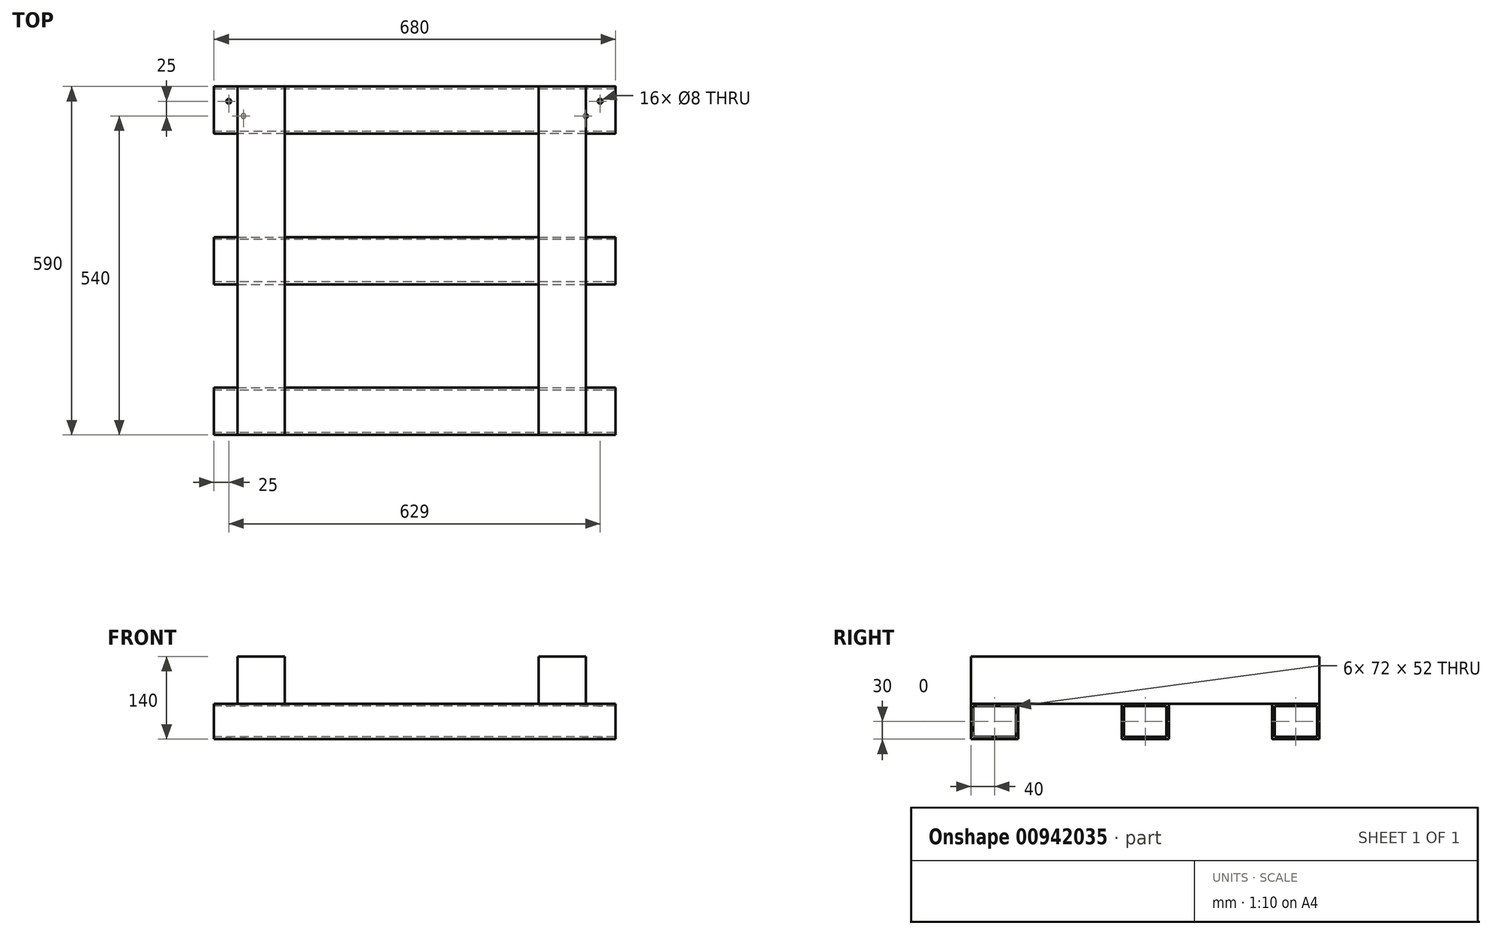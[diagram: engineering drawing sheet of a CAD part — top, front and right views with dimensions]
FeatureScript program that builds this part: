
annotation { "Feature Type Name" : "Feature", "Feature Type Description" : "" }
export const myFeature = defineFeature(function(context is Context, id is Id, definition is map)
    precondition{}
    {
        {
            var Q0;
            Q0=qCreatedBy(makeId("Right.planeOp"),FACE);
            var sketch = newSketch(context, id + "F0", { "sketchPlane" : qUnion([Q0])});
            skLineSegment(sketch, "E0.bottom", {"start": v(40, 30) * mm, "end": v(-40, 30) * mm});
            skLineSegment(sketch, "E0.top", {"start": v(40, -30) * mm, "end": v(-40, -30) * mm});
            skLineSegment(sketch, "E0.left", {"start": v(40, 30) * mm, "end": v(40, -30) * mm});
            skLineSegment(sketch, "E0.right", {"start": v(-40, 30) * mm, "end": v(-40, -30) * mm});
            skPoint(sketch, "E0.middle", {"position": v(0, 0) * mm});
            skSolve(sketch);
        }
        {
            var Q0;
            Q0=qCreatedBy(makeId("Right.planeOp"),FACE);
            var sketch = newSketch(context, id + "F1", { "sketchPlane" : qUnion([Q0])});
            skLineSegment(sketch, "E1.bottom", {"start": v(36, 26) * mm, "end": v(-36, 26) * mm});
            skLineSegment(sketch, "E1.top", {"start": v(36, -26) * mm, "end": v(-36, -26) * mm});
            skLineSegment(sketch, "E1.left", {"start": v(36, 26) * mm, "end": v(36, -26) * mm});
            skLineSegment(sketch, "E1.right", {"start": v(-36, 26) * mm, "end": v(-36, -26) * mm});
            skPoint(sketch, "E1.middle", {"position": v(0, 0) * mm});
            skSolve(sketch);
        }
        {
            var Q0;
            Q0 = qSketchRegion(id + "F0", true);
            extrude(context, id + "F2", {"entities" : qUnion([Q0]), "depth" : 680 * mm, "offsetDistance" : 25.4 * mm});
        }
        {
            var Q0;
            Q0 = qSketchRegion(id + "F1", true);
            extrude(context, id + "F3", {"entities" : qUnion([Q0]), "operationType" : NewBodyOperationType.REMOVE, "endBound" : BoundingType.THROUGH_ALL, "depth" : 600 * mm, "offsetDistance" : 25.4 * mm});
        }
        {
            var Q0;
            Q0=makeQuery(id+"F2.opExtrude","SWEPT_FACE",FACE,{"disambiguationData":[OSD([sQuery(id+"F0.wireOp",EDGE,"E0.right")])]});
            var Q1;
            Q1=makeQuery(id+"F2.opExtrude","SWEPT_FACE",FACE,{"disambiguationData":[OSD([sQuery(id+"F0.wireOp",EDGE,"E0.bottom")])]});
            var Q2;
            Q2=makeQuery(id+"F2.opExtrude","SWEPT_EDGE",EDGE,{"disambiguationData":[OSD([sQuery(id+"F0.wireOp",EDGE,"E0.bottom"),sQuery(id+"F0.wireOp",EDGE,"E0.right")])]});
            var Q3;
            Q3=makeQuery(id+"F2.opExtrude","SWEPT_EDGE",EDGE,{"disambiguationData":[OSD([sQuery(id+"F0.wireOp",EDGE,"E0.bottom"),sQuery(id+"F0.wireOp",EDGE,"E0.left")])]});
            var Q4;
            Q4=makeQuery(id+"F2.opExtrude","SWEPT_EDGE",EDGE,{"disambiguationData":[OSD([sQuery(id+"F0.wireOp",EDGE,"E0.top"),sQuery(id+"F0.wireOp",EDGE,"E0.right")])]});
            var Q5;
            Q5=makeQuery(id+"F2.opExtrude","SWEPT_EDGE",EDGE,{"disambiguationData":[OSD([sQuery(id+"F0.wireOp",EDGE,"E0.top"),sQuery(id+"F0.wireOp",EDGE,"E0.left")])]});
            fillet(context, id + "F4", {"entities" : qUnion([Q0, Q1, Q2, Q3, Q4, Q5]), "radius" : 1 * mm, "tangentPropagation" : true, "allowEdgeOverflow" : false});
        }
        {
            var Q0;
            Q0=makeQuery(id+"F2.opExtrude","SWEPT_FACE",FACE,{"disambiguationData":[OSD([sQuery(id+"F0.wireOp",EDGE,"E0.bottom")])]});
            var sketch = newSketch(context, id + "F5", { "sketchPlane" : qUnion([Q0])});
            skCircle(sketch, "E2", {"center": v(25, 15) * mm, "radius": 4 * mm});
            skCircle(sketch, "E3", {"center": v(50, -10) * mm, "radius": 4 * mm});
            skCircle(sketch, "E4", {"center": v(654, 15) * mm, "radius": 4 * mm});
            skCircle(sketch, "E5", {"center": v(629, -10) * mm, "radius": 4 * mm});
            skSolve(sketch);
        }
        {
            var Q0;
            Q0 = qSketchRegion(id + "F5", true);
            extrude(context, id + "F6", {"entities" : qUnion([Q0]), "operationType" : NewBodyOperationType.REMOVE, "oppositeDirection" : true, "depth" : 254 * mm, "offsetDistance" : 25.4 * mm});
        }
        {
            var Q0;
            Q0=qCreatedBy(makeId("Top.planeOp"),FACE);
            var sketch = newSketch(context, id + "F7", { "sketchPlane" : qUnion([Q0])});
            skLineSegment(sketch, "E6.bottom", {"start": v(0, -470) * mm, "end": v(680, -470) * mm});
            skLineSegment(sketch, "E6.top", {"start": v(0, -550) * mm, "end": v(680, -550) * mm});
            skLineSegment(sketch, "E6.left", {"start": v(0, -470) * mm, "end": v(0, -550) * mm});
            skLineSegment(sketch, "E6.right", {"start": v(680, -470) * mm, "end": v(680, -550) * mm});
            skSolve(sketch);
        }
        {
            var Q0;
            Q0 = qSketchRegion(id + "F7", true);
            extrude(context, id + "F8", {"entities" : qUnion([Q0]), "endBound" : BoundingType.SYMMETRIC, "oppositeDirection" : true, "depth" : 60 * mm, "offsetDistance" : 25.4 * mm});
        }
        {
            var Q0;
            Q0=makeQuery(id+"F8.opExtrude","SWEPT_FACE",FACE,{"disambiguationData":[OSD([sQuery(id+"F7.wireOp",EDGE,"E6.left")])]});
            var sketch = newSketch(context, id + "F9", { "sketchPlane" : qUnion([Q0])});
            skLineSegment(sketch, "E7.bottom", {"start": v(546, 26) * mm, "end": v(474, 26) * mm});
            skLineSegment(sketch, "E7.top", {"start": v(546, -26) * mm, "end": v(474, -26) * mm});
            skLineSegment(sketch, "E7.left", {"start": v(546, 26) * mm, "end": v(546, -26) * mm});
            skLineSegment(sketch, "E7.right", {"start": v(474, 26) * mm, "end": v(474, -26) * mm});
            skPoint(sketch, "E7.middle", {"position": v(510, 0) * mm});
            skSolve(sketch);
        }
        {
            var Q0;
            Q0 = qSketchRegion(id + "F9", true);
            extrude(context, id + "F10", {"entities" : qUnion([Q0]), "operationType" : NewBodyOperationType.REMOVE, "endBound" : BoundingType.THROUGH_ALL, "oppositeDirection" : true, "depth" : 600 * mm, "offsetDistance" : 25.4 * mm});
        }
        {
            var Q0;
            Q0=qCreatedBy(makeId("Top.planeOp"),FACE);
            var sketch = newSketch(context, id + "F11", { "sketchPlane" : qUnion([Q0])});
            skLineSegment(sketch, "E8.bottom", {"start": v(0, -215) * mm, "end": v(680, -215) * mm});
            skLineSegment(sketch, "E8.top", {"start": v(0, -295) * mm, "end": v(680, -295) * mm});
            skLineSegment(sketch, "E8.left", {"start": v(0, -215) * mm, "end": v(0, -295) * mm});
            skLineSegment(sketch, "E8.right", {"start": v(680, -215) * mm, "end": v(680, -295) * mm});
            skSolve(sketch);
        }
        {
            var Q0;
            Q0 = qSketchRegion(id + "F11", true);
            extrude(context, id + "F12", {"entities" : qUnion([Q0]), "endBound" : BoundingType.SYMMETRIC, "depth" : 60 * mm, "offsetDistance" : 25.4 * mm});
        }
        {
            var Q0;
            Q0=makeQuery(id+"F12.opExtrude","SWEPT_FACE",FACE,{"disambiguationData":[OSD([sQuery(id+"F11.wireOp",EDGE,"E8.left")])]});
            var sketch = newSketch(context, id + "F13", { "sketchPlane" : qUnion([Q0])});
            skLineSegment(sketch, "E9.bottom", {"start": v(291, 26) * mm, "end": v(219, 26) * mm});
            skLineSegment(sketch, "E9.top", {"start": v(291, -26) * mm, "end": v(219, -26) * mm});
            skLineSegment(sketch, "E9.left", {"start": v(291, 26) * mm, "end": v(291, -26) * mm});
            skLineSegment(sketch, "E9.right", {"start": v(219, 26) * mm, "end": v(219, -26) * mm});
            skPoint(sketch, "E9.middle", {"position": v(255, 0) * mm});
            skSolve(sketch);
        }
        {
            var Q0;
            Q0 = qSketchRegion(id + "F13", true);
            extrude(context, id + "F14", {"entities" : qUnion([Q0]), "operationType" : NewBodyOperationType.REMOVE, "endBound" : BoundingType.THROUGH_ALL, "oppositeDirection" : true, "depth" : 25.4 * mm, "offsetDistance" : 25.4 * mm});
        }
        {
            var Q0;
            Q0=makeQuery(id+"F8.opExtrude","CAP_FACE",FACE,{"disambiguationData":[OSD([sQuery(id+"F7.wireOp",EDGE,"E6.bottom"),sQuery(id+"F7.wireOp",EDGE,"E6.top"),sQuery(id+"F7.wireOp",EDGE,"E6.left"),sQuery(id+"F7.wireOp",EDGE,"E6.right")])],"isStart":true});
            var sketch = newSketch(context, id + "F15", { "sketchPlane" : qUnion([Q0])});
            skLineSegment(sketch, "E10.bottom", {"start": v(40, -550) * mm, "end": v(120, -550) * mm});
            skLineSegment(sketch, "E10.top", {"start": v(40, 40) * mm, "end": v(120, 40) * mm});
            skLineSegment(sketch, "E10.left", {"start": v(40, -550) * mm, "end": v(40, 40) * mm});
            skLineSegment(sketch, "E10.right", {"start": v(120, -550) * mm, "end": v(120, 40) * mm});
            skLineSegment(sketch, "E11.bottom", {"start": v(630, -550) * mm, "end": v(550, -550) * mm});
            skLineSegment(sketch, "E11.top", {"start": v(630, 40) * mm, "end": v(550, 40) * mm});
            skLineSegment(sketch, "E11.left", {"start": v(630, -550) * mm, "end": v(630, 40) * mm});
            skLineSegment(sketch, "E11.right", {"start": v(550, -550) * mm, "end": v(550, 40) * mm});
            skSolve(sketch);
        }
        {
            var Q0;
            Q0 = qSketchRegion(id + "F15", true);
            extrude(context, id + "F16", {"entities" : qUnion([Q0]), "depth" : 80 * mm, "offsetDistance" : 25.4 * mm});
        }
    });
